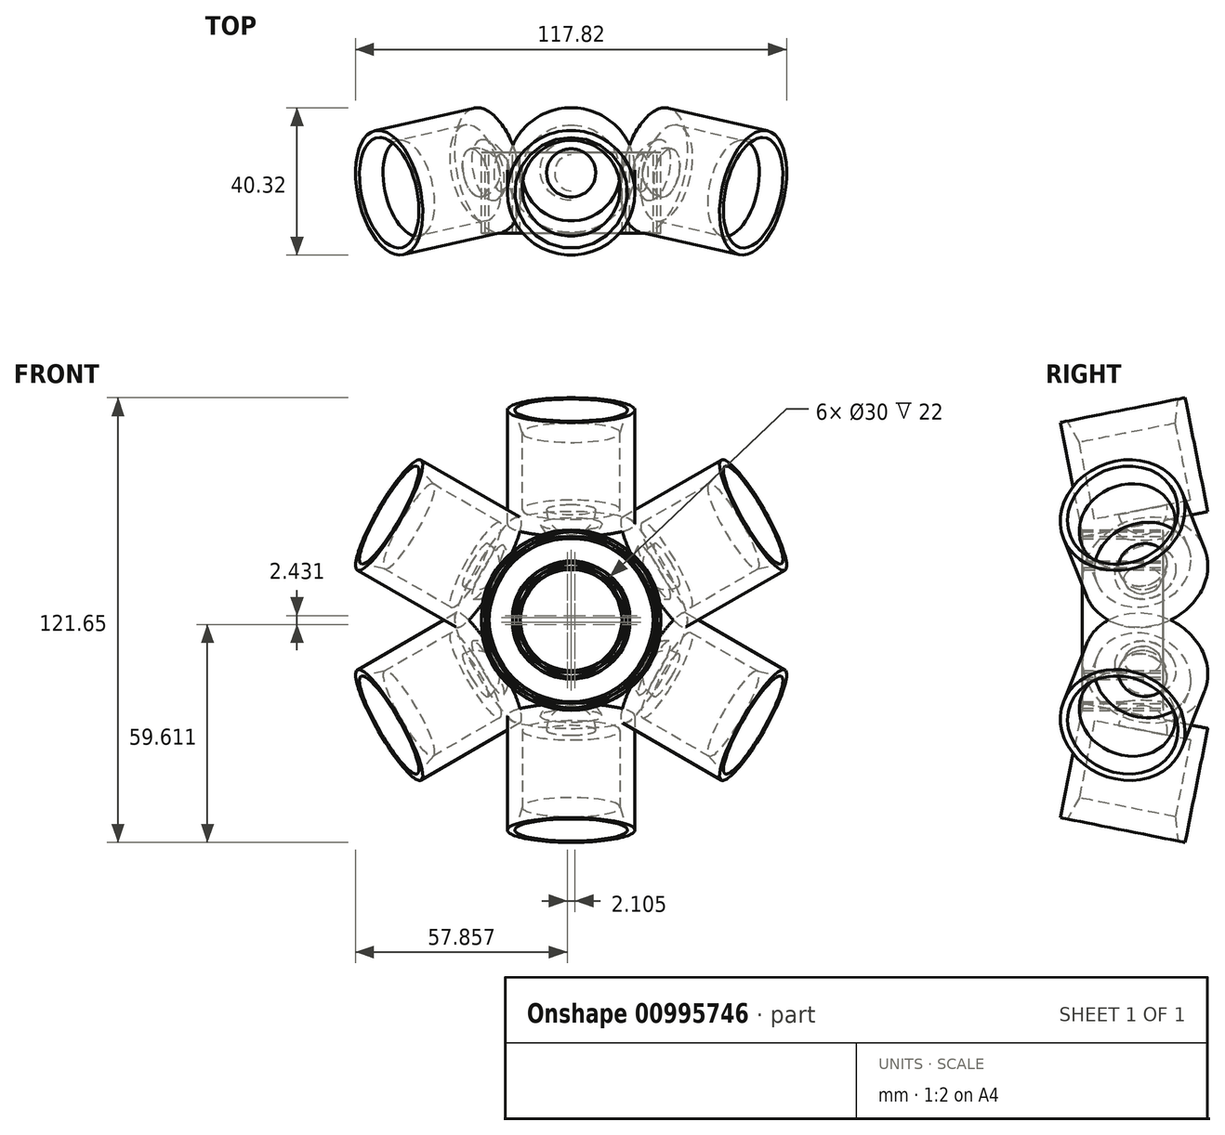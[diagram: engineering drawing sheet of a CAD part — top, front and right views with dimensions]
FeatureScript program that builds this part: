
annotation { "Feature Type Name" : "Feature", "Feature Type Description" : "" }
export const myFeature = defineFeature(function(context is Context, id is Id, definition is map)
    precondition{}
    {
        {
            var Q0;
            Q0=qCreatedBy(makeId("Front.planeOp"),FACE);
            var sketch = newSketch(context, id + "F0", { "sketchPlane" : qUnion([Q0])});
            skPoint(sketch, "E0.middle", {"position": v(0, 0) * mm});
            skPoint(sketch, "E1", {"position": v(0, 43.11) * mm});
            skCircle(sketch, "E2", {"center": v(0, 43.11) * mm, "radius": 23.5 * mm});
            skCircle(sketch, "E3", {"center": v(0, 43.11) * mm, "radius": 15 * mm});
            skLineSegment(sketch, "E4", {"start": v(0, 77.35) * mm, "end": v(0, -6.47) * mm, "construction": true});
            skPoint(sketch, "E5", {"position": v(0, 19.61) * mm});
            skLineSegment(sketch, "E6", {"start": v(26.39, 19.61) * mm, "end": v(-30.99, 19.61) * mm, "construction": true});
            skSolve(sketch);
        }
        {
            var Q0;
            Q0=sQuery(id+"F0.wireOp",EDGE,"E6");
            cPlane(context, id + "F1", {"entities" : qUnion([Q0]), "cplaneType" : CPlaneType.LINE_ANGLE, "offset" : 25 * mm, "angle" : 11.25 * degree, "width" : 150 * mm, "height" : 150 * mm});
        }
        {
            var Q0;
            Q0=qCreatedBy(id+"F1.planeOp",FACE);
            var sketch = newSketch(context, id + "F2", { "sketchPlane" : qUnion([Q0])});
            skPoint(sketch, "E7.middle", {"position": v(-6.69, -12.3) * mm});
            skLineSegment(sketch, "E8", {"start": v(8.7, -27.2) * mm, "end": v(10.7, -27.2) * mm});
            skPoint(sketch, "E9.end.orphan", {"position": v(6.7, -27.2) * mm});
            skPoint(sketch, "E10", {"position": v(-6.69, 29.59) * mm});
            skLineSegment(sketch, "E11.right", {"start": v(13.39, 11.2) * mm, "end": v(13.39, -10.25) * mm});
            skArc(sketch, "E12", {"start": v(6.73, 11.2) * mm, "mid": v(4.76, 15.95) * mm, "end": v(0, 17.92) * mm});
            skArc(sketch, "E13", {"start": v(8.47, 15.2) * mm, "mid": v(5.01, 19.1) * mm, "end": v(0, 20.56) * mm});
            skLineSegment(sketch, "E14", {"start": v(17.39, 15.2) * mm, "end": v(17.39, -16.6) * mm});
            skLineSegment(sketch, "E15", {"start": v(15.39, -16.6) * mm, "end": v(17.39, -16.6) * mm});
            skLineSegment(sketch, "E16", {"start": v(17.39, 15.2) * mm, "end": v(8.47, 15.2) * mm});
            skLineSegment(sketch, "E17", {"start": v(15.39, -16.6) * mm, "end": v(13.39, -10.25) * mm});
            skLineSegment(sketch, "E18", {"start": v(13.39, 11.2) * mm, "end": v(6.73, 11.2) * mm});
            skLineSegment(sketch, "E19", {"start": v(0, 17.92) * mm, "end": v(0, 20.56) * mm});
            skSolve(sketch);
        }
        {
            var Q0;
            Q0=makeQuery(id+"F2.imprint","IMPRINT",FACE,{"disambiguationData":[TD([[makeQuery(id+"F2.imprint","IMPRINT",EDGE,{"derivedFrom":sQuery(id+"F2.wireOp",EDGE,"E11.right")}),1.0]])]});
            var Q1;
            Q1=sQuery(id+"F2.wireOp",EDGE,"E19");
            revolve(context, id + "F3", {"surfaceOperationType" : NewSurfaceOperationType.NEW, "entities" : qUnion([Q0]), "axis" : qUnion([Q1]), "revolveType" : RevolveType.FULL});
        }
        {
            var Q0;
            Q0=makeQuery(id+"F0.imprint","IMPRINT",FACE,{"disambiguationData":[TD([[makeQuery(id+"F0.imprint","IMPRINT",EDGE,{"derivedFrom":sQuery(id+"F0.wireOp",EDGE,"E2")}),1.0]])]});
            extrude(context, id + "F4", {"entities" : qUnion([Q0]), "operationType" : NewBodyOperationType.ADD, "depth" : 18 * mm, "offsetDistance" : 25 * mm, "hasSecondDirection" : true, "secondDirectionOppositeDirection" : true, "secondDirectionDepth" : 4 * mm});
        }
        {
            var Q0;
            Q0=qCreatedBy(makeId("Right.planeOp"),FACE);
            var sketch = newSketch(context, id + "F5", { "sketchPlane" : qUnion([Q0])});
            skLineSegment(sketch, "E20", {"start": v(-35.17, 41.9) * mm, "end": v(25.33, 41.9) * mm, "construction": true});
            skSolve(sketch);
        }
        {
            var Q0;
            Q0=makeQuery(id+"F3.opRevolve","SWEPT_BODY",BODY,{"disambiguationData":[OSD([sQuery(id+"F2.wireOp",EDGE,"E11.right"),sQuery(id+"F2.wireOp",EDGE,"E12"),sQuery(id+"F2.wireOp",EDGE,"E13"),sQuery(id+"F2.wireOp",EDGE,"E14"),sQuery(id+"F2.wireOp",EDGE,"E15"),sQuery(id+"F2.wireOp",EDGE,"E16"),sQuery(id+"F2.wireOp",EDGE,"E17"),sQuery(id+"F2.wireOp",EDGE,"E18"),sQuery(id+"F2.wireOp",EDGE,"E19")])]});
            var Q1;
            Q1=sQuery(id+"F5.wireOp",EDGE,"E20");
            circularPattern(context, id + "F6", {"entities" : qUnion([Q0]), "axis" : qUnion([Q1]), "angle" : 360 * degree, "instanceCount" : 6, "equalSpace" : true});
        }
    });
